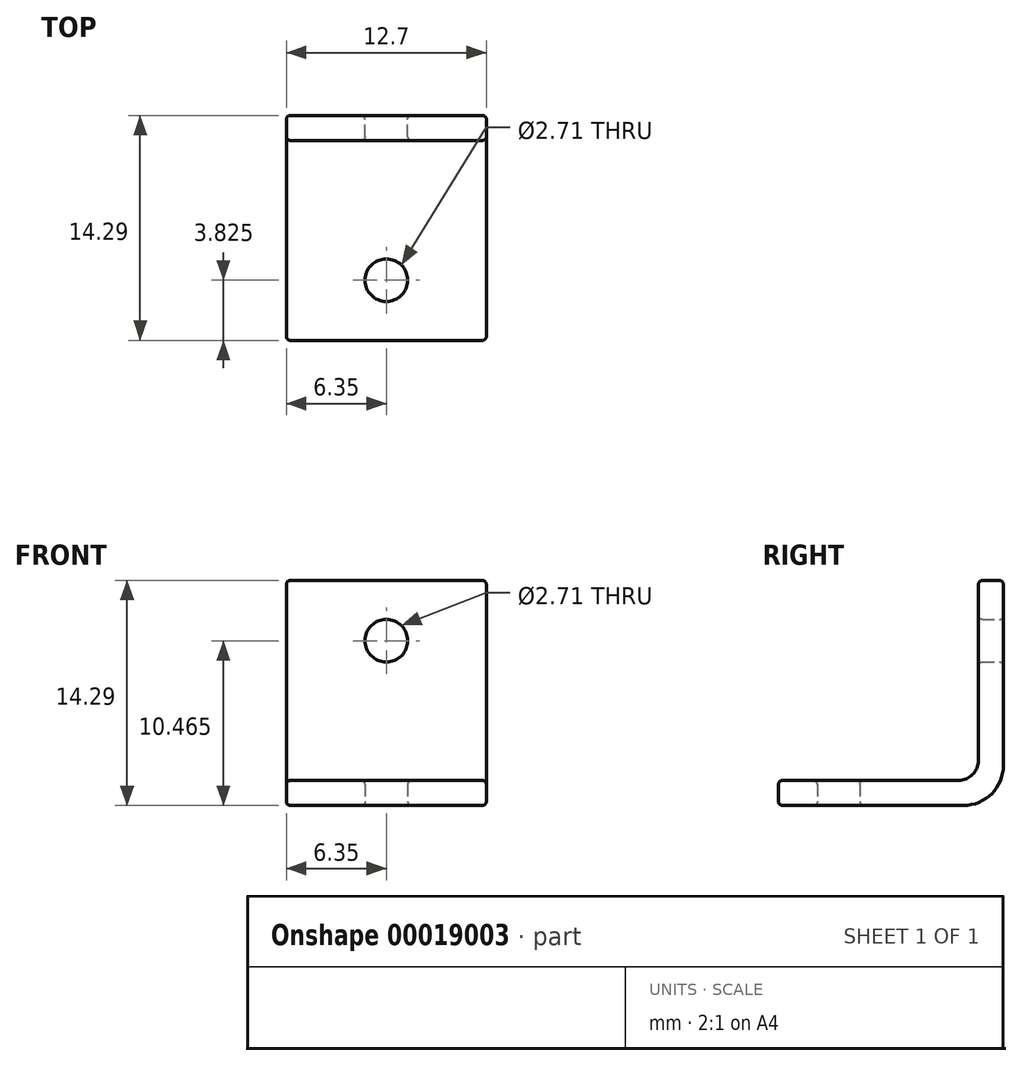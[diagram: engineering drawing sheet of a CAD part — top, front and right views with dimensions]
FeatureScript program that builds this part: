
annotation { "Feature Type Name" : "Feature", "Feature Type Description" : "" }
export const myFeature = defineFeature(function(context is Context, id is Id, definition is map)
    precondition{}
    {
        {
            var Q0;
            Q0=qCreatedBy(makeId("Front.planeOp"),FACE);
            var sketch = newSketch(context, id + "F0", { "sketchPlane" : qUnion([Q0])});
            skLineSegment(sketch, "E0.bottom", {"start": v(-6.35, 14.29) * mm, "end": v(6.35, 14.29) * mm});
            skLineSegment(sketch, "E0.top", {"start": v(-6.35, 0) * mm, "end": v(6.35, 0) * mm});
            skLineSegment(sketch, "E0.left", {"start": v(-6.35, 14.29) * mm, "end": v(-6.35, 0) * mm});
            skLineSegment(sketch, "E0.right", {"start": v(6.35, 14.29) * mm, "end": v(6.35, 0) * mm});
            skLineSegment(sketch, "E1", {"start": v(-6.35, 1.59) * mm, "end": v(6.35, 1.59) * mm});
            skCircle(sketch, "E2", {"center": v(0, 10.46) * mm, "radius": 1.35 * mm});
            skSolve(sketch);
        }
        {
            var Q0;
            Q0 = qSketchRegion(id + "F0", true);
            extrude(context, id + "F1", {"entities" : qUnion([Q0]), "depth" : 1.59 * mm});
        }
        {
            var Q0;
            {var subQ2=sQuery(id+"F0.wireOp",EDGE,"E0.top");Q0=makeQuery(id+"F0.imprint","IMPRINT",FACE,{"disambiguationData":[TD([[makeQuery(id+"F0.imprint","IMPRINT",EDGE,{"derivedFrom":subQ2}),1.0]])]});}
            extrude(context, id + "F2", {"entities" : qUnion([Q0]), "operationType" : NewBodyOperationType.ADD, "depth" : 14.29 * mm});
        }
        {
            var Q0;
            {var subQ0=sQuery(id+"F0.wireOp",EDGE,"E0.top");Q0=makeQuery(id+"F2.boolean.opBoolean","MERGE",FACE,{"derivedFrom":[makeQuery(id+"F1.opExtrude","SWEPT_FACE",FACE,{"disambiguationData":[OSD([subQ0])]}),makeQuery(id+"F2.opExtrude","SWEPT_FACE",FACE,{"disambiguationData":[OSD([subQ0])]})]});}
            var sketch = newSketch(context, id + "F3", { "sketchPlane" : qUnion([Q0])});
            skCircle(sketch, "E3", {"center": v(0, 10.46) * mm, "radius": 1.35 * mm});
            skSolve(sketch);
        }
        {
            var Q0;
            Q0 = qSketchRegion(id + "F3", true);
            extrude(context, id + "F4", {"entities" : qUnion([Q0]), "operationType" : NewBodyOperationType.REMOVE, "endBound" : BoundingType.UP_TO_NEXT, "oppositeDirection" : true, "depth" : 25.4 * mm});
        }
        {
            var Q0;
            Q0=makeQuery(id+"F1.opExtrude","CAP_EDGE",EDGE,{"disambiguationData":[OSD([sQuery(id+"F0.wireOp",EDGE,"E0.top")])],"isStart":true});
            fillet(context, id + "F5", {"entities" : qUnion([Q0]), "radius" : 2.54 * mm, "tangentPropagation" : true, "allowEdgeOverflow" : false});
        }
        {
            var Q0;
            Q0=makeQuery(id+"F2.boolean.opBoolean","INTERSECT",EDGE,{"derivedFrom":[makeQuery(id+"F1.opExtrude","CAP_FACE",FACE,{"disambiguationData":[OSD([sQuery(id+"F0.wireOp",EDGE,"E0.bottom"),sQuery(id+"F0.wireOp",EDGE,"E0.top"),sQuery(id+"F0.wireOp",EDGE,"E0.left"),sQuery(id+"F0.wireOp",EDGE,"E0.right"),sQuery(id+"F0.wireOp",EDGE,"E2")])],"isStart":false}),makeQuery(id+"F2.opExtrude","SWEPT_FACE",FACE,{"disambiguationData":[OSD([sQuery(id+"F0.wireOp",EDGE,"E1")])]})]});
            fillet(context, id + "F6", {"entities" : qUnion([Q0]), "radius" : 1.27 * mm, "tangentPropagation" : true, "allowEdgeOverflow" : false});
        }
        {
            var Q0;
            {var subQ0=sQuery(id+"F0.wireOp",EDGE,"E0.right");Q0=makeQuery(id+"F2.boolean.opBoolean","MERGE",FACE,{"derivedFrom":[makeQuery(id+"F1.opExtrude","SWEPT_FACE",FACE,{"disambiguationData":[OSD([subQ0])]}),makeQuery(id+"F2.opExtrude","SWEPT_FACE",FACE,{"disambiguationData":[OSD([subQ0])]})]});}
            var Q1;
            {var subQ0=sQuery(id+"F0.wireOp",EDGE,"E0.left");Q1=makeQuery(id+"F2.boolean.opBoolean","MERGE",FACE,{"derivedFrom":[makeQuery(id+"F1.opExtrude","SWEPT_FACE",FACE,{"disambiguationData":[OSD([subQ0])]}),makeQuery(id+"F2.opExtrude","SWEPT_FACE",FACE,{"disambiguationData":[OSD([subQ0])]})]});}
            var Q2;
            Q2=makeQuery(id+"F1.opExtrude","SWEPT_FACE",FACE,{"disambiguationData":[OSD([sQuery(id+"F0.wireOp",EDGE,"E0.bottom")])]});
            var Q3;
            Q3=makeQuery(id+"F5.opFillet","BLEND_FACE",FACE,{"disambiguationData":[OSD([sQuery(id+"F0.wireOp",EDGE,"E0.bottom"),sQuery(id+"F0.wireOp",EDGE,"E0.top"),sQuery(id+"F0.wireOp",EDGE,"E0.left"),sQuery(id+"F0.wireOp",EDGE,"E0.right"),sQuery(id+"F0.wireOp",EDGE,"E1"),sQuery(id+"F0.wireOp",EDGE,"E2")])]});
            var Q4;
            Q4=makeQuery(id+"F2.opExtrude","SWEPT_FACE",FACE,{"disambiguationData":[OSD([sQuery(id+"F0.wireOp",EDGE,"E1")])]});
            var Q5;
            Q5=makeQuery(id+"F2.opExtrude","CAP_EDGE",EDGE,{"disambiguationData":[OSD([sQuery(id+"F0.wireOp",EDGE,"E0.top")])],"isStart":false});
            var Q6;
            Q6=makeQuery(id+"F1.opExtrude","CAP_FACE",FACE,{"disambiguationData":[OSD([sQuery(id+"F0.wireOp",EDGE,"E0.bottom"),sQuery(id+"F0.wireOp",EDGE,"E0.top"),sQuery(id+"F0.wireOp",EDGE,"E0.left"),sQuery(id+"F0.wireOp",EDGE,"E0.right"),sQuery(id+"F0.wireOp",EDGE,"E2")])],"isStart":false});
            var Q7;
            Q7=makeQuery(id+"F1.opExtrude","CAP_FACE",FACE,{"disambiguationData":[OSD([sQuery(id+"F0.wireOp",EDGE,"E0.bottom"),sQuery(id+"F0.wireOp",EDGE,"E0.top"),sQuery(id+"F0.wireOp",EDGE,"E0.left"),sQuery(id+"F0.wireOp",EDGE,"E0.right"),sQuery(id+"F0.wireOp",EDGE,"E2")])],"isStart":true});
            var Q8;
            {var subQ0=sQuery(id+"F0.wireOp",EDGE,"E0.top");Q8=makeQuery(id+"F2.boolean.opBoolean","MERGE",FACE,{"derivedFrom":[makeQuery(id+"F1.opExtrude","SWEPT_FACE",FACE,{"disambiguationData":[OSD([subQ0])]}),makeQuery(id+"F2.opExtrude","SWEPT_FACE",FACE,{"disambiguationData":[OSD([subQ0])]})]});}
            var Q9;
            Q9=makeQuery(id+"F5.opFillet","BLEND_FACE",FACE,{"disambiguationData":[OSD([sQuery(id+"F0.wireOp",EDGE,"E0.top")])]});
            fillet(context, id + "F7", {"entities" : qUnion([Q0, Q1, Q2, Q3, Q4, Q5, Q6, Q7, Q8, Q9]), "radius" : 0.25 * mm, "tangentPropagation" : true, "allowEdgeOverflow" : false});
        }
        {
            var Q0;
            {var subQ0=sQuery(id+"F0.wireOp",EDGE,"E0.top");Q0=makeQuery(id+"F2.boolean.opBoolean","MERGE",FACE,{"derivedFrom":[makeQuery(id+"F1.opExtrude","SWEPT_FACE",FACE,{"disambiguationData":[OSD([subQ0])]}),makeQuery(id+"F2.opExtrude","SWEPT_FACE",FACE,{"disambiguationData":[OSD([subQ0])]})]});}
            var sketch = newSketch(context, id + "F8", { "sketchPlane" : qUnion([Q0])});
            skLineSegment(sketch, "E4.0", {"start": v(6.1, 0) * mm, "end": v(-6.1, 0) * mm});
            skSolve(sketch);
        }
    });
